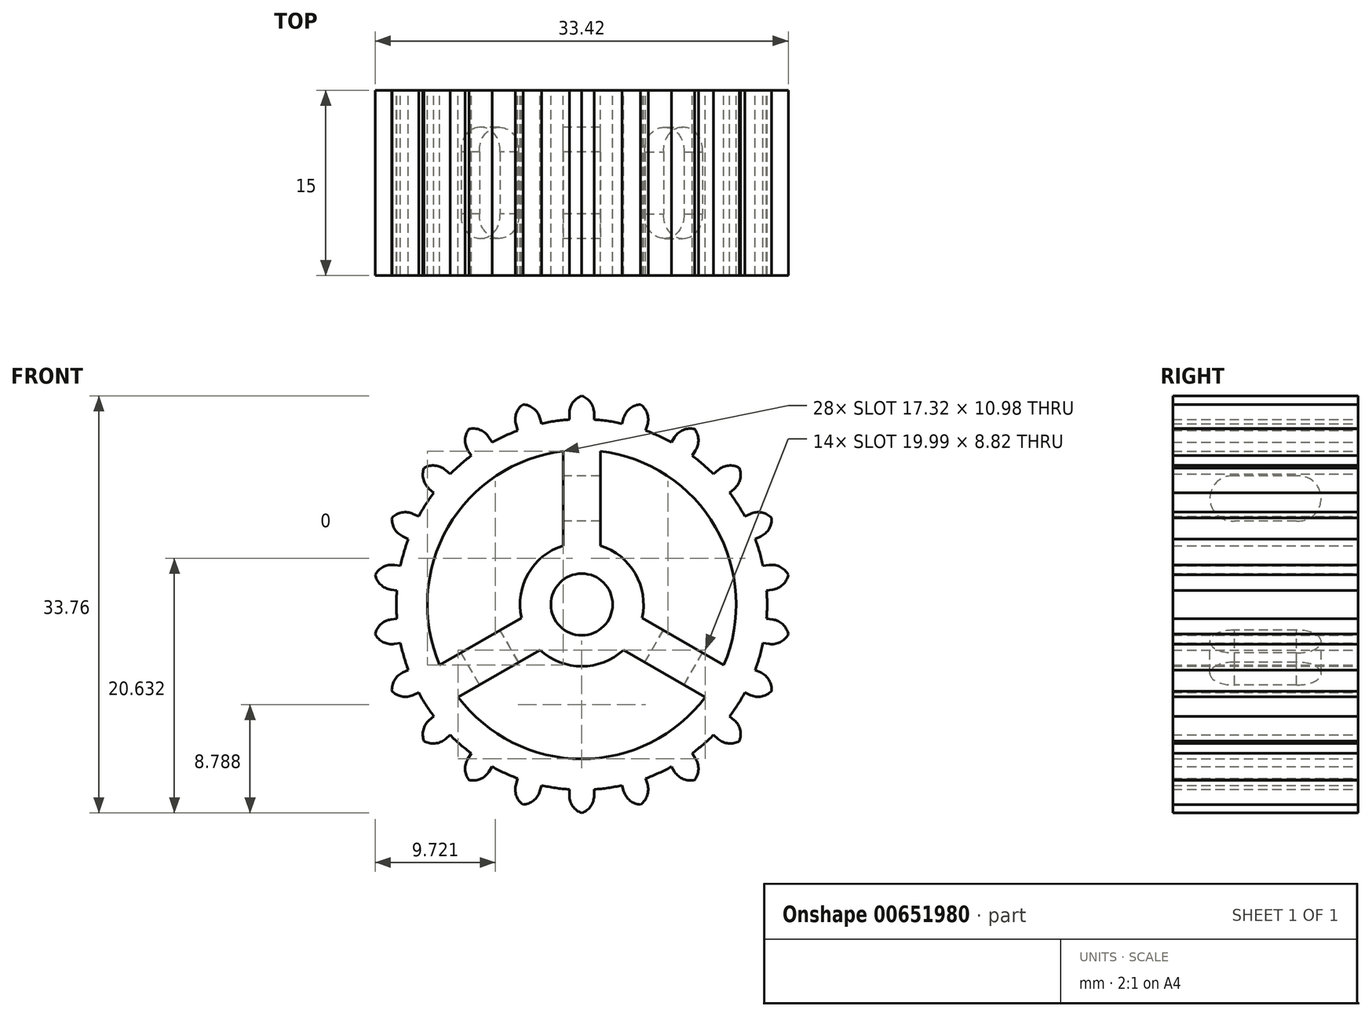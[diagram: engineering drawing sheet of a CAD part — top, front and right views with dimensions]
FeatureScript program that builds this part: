
annotation { "Feature Type Name" : "Feature", "Feature Type Description" : "" }
export const myFeature = defineFeature(function(context is Context, id is Id, definition is map)
    precondition{}
    {
        {
            var Q0;
            Q0=qCreatedBy(makeId("Front.planeOp"),FACE);
            var sketch = newSketch(context, id + "F0", { "sketchPlane" : qUnion([Q0])});
            skArc(sketch, "E0", {"start": v(-1, 14.97) * mm, "mid": v(-2.13, 14.85) * mm, "end": v(-3.26, 14.64) * mm});
            skLineSegment(sketch, "E1", {"start": v(-1, 14.97) * mm, "end": v(-1, 16.97) * mm});
            skLineSegment(sketch, "E2", {"start": v(-1, 16.97) * mm, "end": v(1, 16.97) * mm});
            skLineSegment(sketch, "E3", {"start": v(1, 16.97) * mm, "end": v(1, 14.97) * mm});
            skLineSegment(sketch, "E4.1.0", {"start": v(-3.82, 16.56) * mm, "end": v(-3.26, 14.64) * mm});
            skLineSegment(sketch, "E4.1.1", {"start": v(-5.18, 14.08) * mm, "end": v(-5.74, 16) * mm});
            skLineSegment(sketch, "E4.1.2", {"start": v(-5.74, 16) * mm, "end": v(-3.82, 16.56) * mm});
            skLineSegment(sketch, "E4.2.0", {"start": v(-8.33, 14.81) * mm, "end": v(-7.25, 13.13) * mm});
            skLineSegment(sketch, "E4.2.1", {"start": v(-8.93, 12.05) * mm, "end": v(-10.01, 13.73) * mm});
            skLineSegment(sketch, "E4.2.2", {"start": v(-10.01, 13.73) * mm, "end": v(-8.33, 14.81) * mm});
            skLineSegment(sketch, "E4.3.0", {"start": v(-12.17, 11.87) * mm, "end": v(-10.66, 10.56) * mm});
            skLineSegment(sketch, "E4.3.1", {"start": v(-11.97, 9.05) * mm, "end": v(-13.48, 10.36) * mm});
            skLineSegment(sketch, "E4.3.2", {"start": v(-13.48, 10.36) * mm, "end": v(-12.17, 11.87) * mm});
            skLineSegment(sketch, "E4.4.0", {"start": v(-15.02, 7.96) * mm, "end": v(-13.2, 7.13) * mm});
            skLineSegment(sketch, "E4.4.1", {"start": v(-14.03, 5.3) * mm, "end": v(-15.85, 6.14) * mm});
            skLineSegment(sketch, "E4.4.2", {"start": v(-15.85, 6.14) * mm, "end": v(-15.02, 7.96) * mm});
            skLineSegment(sketch, "E4.5.0", {"start": v(-16.65, 3.4) * mm, "end": v(-14.67, 3.12) * mm});
            skLineSegment(sketch, "E4.5.1", {"start": v(-14.96, 1.14) * mm, "end": v(-16.94, 1.42) * mm});
            skLineSegment(sketch, "E4.5.2", {"start": v(-16.94, 1.42) * mm, "end": v(-16.65, 3.4) * mm});
            skLineSegment(sketch, "E4.6.0", {"start": v(-16.94, -1.42) * mm, "end": v(-14.96, -1.14) * mm});
            skLineSegment(sketch, "E4.6.1", {"start": v(-14.67, -3.12) * mm, "end": v(-16.65, -3.4) * mm});
            skLineSegment(sketch, "E4.6.2", {"start": v(-16.65, -3.4) * mm, "end": v(-16.94, -1.42) * mm});
            skLineSegment(sketch, "E4.7.0", {"start": v(-15.85, -6.14) * mm, "end": v(-14.03, -5.3) * mm});
            skLineSegment(sketch, "E4.7.1", {"start": v(-13.2, -7.13) * mm, "end": v(-15.02, -7.96) * mm});
            skLineSegment(sketch, "E4.7.2", {"start": v(-15.02, -7.96) * mm, "end": v(-15.85, -6.14) * mm});
            skLineSegment(sketch, "E4.8.0", {"start": v(-13.48, -10.36) * mm, "end": v(-11.97, -9.05) * mm});
            skLineSegment(sketch, "E4.8.1", {"start": v(-10.66, -10.56) * mm, "end": v(-12.17, -11.87) * mm});
            skLineSegment(sketch, "E4.8.2", {"start": v(-12.17, -11.87) * mm, "end": v(-13.48, -10.36) * mm});
            skLineSegment(sketch, "E4.9.0", {"start": v(-10.01, -13.73) * mm, "end": v(-8.93, -12.05) * mm});
            skLineSegment(sketch, "E4.9.1", {"start": v(-7.25, -13.13) * mm, "end": v(-8.33, -14.81) * mm});
            skLineSegment(sketch, "E4.9.2", {"start": v(-8.33, -14.81) * mm, "end": v(-10.01, -13.73) * mm});
            skLineSegment(sketch, "E4.10.0", {"start": v(-5.74, -16) * mm, "end": v(-5.18, -14.08) * mm});
            skLineSegment(sketch, "E4.10.1", {"start": v(-3.26, -14.64) * mm, "end": v(-3.82, -16.56) * mm});
            skLineSegment(sketch, "E4.10.2", {"start": v(-3.82, -16.56) * mm, "end": v(-5.74, -16) * mm});
            skLineSegment(sketch, "E4.11.0", {"start": v(-1, -16.97) * mm, "end": v(-1, -14.97) * mm});
            skLineSegment(sketch, "E4.11.1", {"start": v(1, -14.97) * mm, "end": v(1, -16.97) * mm});
            skLineSegment(sketch, "E4.11.2", {"start": v(1, -16.97) * mm, "end": v(-1, -16.97) * mm});
            skLineSegment(sketch, "E4.12.0", {"start": v(3.82, -16.56) * mm, "end": v(3.26, -14.64) * mm});
            skLineSegment(sketch, "E4.12.1", {"start": v(5.18, -14.08) * mm, "end": v(5.74, -16) * mm});
            skLineSegment(sketch, "E4.12.2", {"start": v(5.74, -16) * mm, "end": v(3.82, -16.56) * mm});
            skLineSegment(sketch, "E4.13.0", {"start": v(8.33, -14.81) * mm, "end": v(7.25, -13.13) * mm});
            skLineSegment(sketch, "E4.13.1", {"start": v(8.93, -12.05) * mm, "end": v(10.01, -13.73) * mm});
            skLineSegment(sketch, "E4.13.2", {"start": v(10.01, -13.73) * mm, "end": v(8.33, -14.81) * mm});
            skLineSegment(sketch, "E4.14.0", {"start": v(12.17, -11.87) * mm, "end": v(10.66, -10.56) * mm});
            skLineSegment(sketch, "E4.14.1", {"start": v(11.97, -9.05) * mm, "end": v(13.48, -10.36) * mm});
            skLineSegment(sketch, "E4.14.2", {"start": v(13.48, -10.36) * mm, "end": v(12.17, -11.87) * mm});
            skLineSegment(sketch, "E4.15.0", {"start": v(15.02, -7.96) * mm, "end": v(13.2, -7.13) * mm});
            skLineSegment(sketch, "E4.15.1", {"start": v(14.03, -5.3) * mm, "end": v(15.85, -6.14) * mm});
            skLineSegment(sketch, "E4.15.2", {"start": v(15.85, -6.14) * mm, "end": v(15.02, -7.96) * mm});
            skLineSegment(sketch, "E4.16.0", {"start": v(16.65, -3.4) * mm, "end": v(14.67, -3.12) * mm});
            skLineSegment(sketch, "E4.16.1", {"start": v(14.96, -1.14) * mm, "end": v(16.94, -1.42) * mm});
            skLineSegment(sketch, "E4.16.2", {"start": v(16.94, -1.42) * mm, "end": v(16.65, -3.4) * mm});
            skLineSegment(sketch, "E4.17.0", {"start": v(16.94, 1.42) * mm, "end": v(14.96, 1.14) * mm});
            skLineSegment(sketch, "E4.17.1", {"start": v(14.67, 3.12) * mm, "end": v(16.65, 3.4) * mm});
            skLineSegment(sketch, "E4.17.2", {"start": v(16.65, 3.4) * mm, "end": v(16.94, 1.42) * mm});
            skLineSegment(sketch, "E4.18.0", {"start": v(15.85, 6.14) * mm, "end": v(14.03, 5.3) * mm});
            skLineSegment(sketch, "E4.18.1", {"start": v(13.2, 7.13) * mm, "end": v(15.02, 7.96) * mm});
            skLineSegment(sketch, "E4.18.2", {"start": v(15.02, 7.96) * mm, "end": v(15.85, 6.14) * mm});
            skLineSegment(sketch, "E4.19.0", {"start": v(13.48, 10.36) * mm, "end": v(11.97, 9.05) * mm});
            skLineSegment(sketch, "E4.19.1", {"start": v(10.66, 10.56) * mm, "end": v(12.17, 11.87) * mm});
            skLineSegment(sketch, "E4.19.2", {"start": v(12.17, 11.87) * mm, "end": v(13.48, 10.36) * mm});
            skLineSegment(sketch, "E4.20.0", {"start": v(10.01, 13.73) * mm, "end": v(8.93, 12.05) * mm});
            skLineSegment(sketch, "E4.20.1", {"start": v(7.25, 13.13) * mm, "end": v(8.33, 14.81) * mm});
            skLineSegment(sketch, "E4.20.2", {"start": v(8.33, 14.81) * mm, "end": v(10.01, 13.73) * mm});
            skLineSegment(sketch, "E4.21.0", {"start": v(5.74, 16) * mm, "end": v(5.18, 14.08) * mm});
            skLineSegment(sketch, "E4.21.1", {"start": v(3.26, 14.64) * mm, "end": v(3.82, 16.56) * mm});
            skLineSegment(sketch, "E4.21.2", {"start": v(3.82, 16.56) * mm, "end": v(5.74, 16) * mm});
            skArc(sketch, "E5.trimOffspring", {"start": v(3.26, 14.64) * mm, "mid": v(2.13, 14.85) * mm, "end": v(1, 14.97) * mm});
            skArc(sketch, "E6.trimOffspring", {"start": v(7.25, 13.13) * mm, "mid": v(6.23, 13.64) * mm, "end": v(5.18, 14.08) * mm});
            skArc(sketch, "E7.trimOffspring", {"start": v(10.66, 10.56) * mm, "mid": v(9.82, 11.34) * mm, "end": v(8.93, 12.05) * mm});
            skArc(sketch, "E8.trimOffspring", {"start": v(13.2, 7.13) * mm, "mid": v(12.62, 8.1) * mm, "end": v(11.97, 9.05) * mm});
            skArc(sketch, "E9.trimOffspring", {"start": v(14.67, 3.12) * mm, "mid": v(14.4, 4.23) * mm, "end": v(14.03, 5.3) * mm});
            skArc(sketch, "E10.trimOffspring", {"start": v(14.96, -1.14) * mm, "mid": v(15, 0) * mm, "end": v(14.96, 1.14) * mm});
            skArc(sketch, "E11.trimOffspring", {"start": v(14.03, -5.3) * mm, "mid": v(14.4, -4.23) * mm, "end": v(14.67, -3.12) * mm});
            skArc(sketch, "E12.trimOffspring", {"start": v(11.97, -9.05) * mm, "mid": v(12.62, -8.1) * mm, "end": v(13.2, -7.13) * mm});
            skArc(sketch, "E13.trimOffspring", {"start": v(8.93, -12.05) * mm, "mid": v(9.82, -11.34) * mm, "end": v(10.66, -10.56) * mm});
            skArc(sketch, "E14.trimOffspring", {"start": v(5.18, -14.08) * mm, "mid": v(6.23, -13.64) * mm, "end": v(7.25, -13.13) * mm});
            skArc(sketch, "E15.trimOffspring", {"start": v(1, -14.97) * mm, "mid": v(2.13, -14.85) * mm, "end": v(3.26, -14.64) * mm});
            skArc(sketch, "E16.trimOffspring", {"start": v(-3.26, -14.64) * mm, "mid": v(-2.13, -14.85) * mm, "end": v(-1, -14.97) * mm});
            skArc(sketch, "E17.trimOffspring", {"start": v(-7.25, -13.13) * mm, "mid": v(-6.23, -13.64) * mm, "end": v(-5.18, -14.08) * mm});
            skArc(sketch, "E18.trimOffspring", {"start": v(-10.66, -10.56) * mm, "mid": v(-9.82, -11.34) * mm, "end": v(-8.93, -12.05) * mm});
            skArc(sketch, "E19.trimOffspring", {"start": v(-13.2, -7.13) * mm, "mid": v(-12.62, -8.1) * mm, "end": v(-11.97, -9.05) * mm});
            skArc(sketch, "E20.trimOffspring", {"start": v(-14.67, -3.12) * mm, "mid": v(-14.4, -4.23) * mm, "end": v(-14.03, -5.3) * mm});
            skArc(sketch, "E21.trimOffspring", {"start": v(-14.96, 1.14) * mm, "mid": v(-15, 0) * mm, "end": v(-14.96, -1.14) * mm});
            skArc(sketch, "E22.trimOffspring", {"start": v(-14.03, 5.3) * mm, "mid": v(-14.4, 4.23) * mm, "end": v(-14.67, 3.12) * mm});
            skArc(sketch, "E23.trimOffspring", {"start": v(-11.97, 9.05) * mm, "mid": v(-12.62, 8.1) * mm, "end": v(-13.2, 7.13) * mm});
            skArc(sketch, "E24.trimOffspring", {"start": v(-8.93, 12.05) * mm, "mid": v(-9.82, 11.34) * mm, "end": v(-10.66, 10.56) * mm});
            skArc(sketch, "E25.trimOffspring", {"start": v(-5.18, 14.08) * mm, "mid": v(-6.23, 13.64) * mm, "end": v(-7.25, 13.13) * mm});
            skCircle(sketch, "E26", {"center": v(0, 0) * mm, "radius": 2.5 * mm});
            skArc(sketch, "E27", {"start": v(-1.5, 12.4) * mm, "mid": v(-10.83, 6.25) * mm, "end": v(-11.5, -4.9) * mm});
            skLineSegment(sketch, "E28", {"start": v(-1.5, 4.77) * mm, "end": v(-1.5, 12.4) * mm});
            skLineSegment(sketch, "E29", {"start": v(1.5, 12.4) * mm, "end": v(1.5, 4.77) * mm});
            skLineSegment(sketch, "E30.1.0", {"start": v(-3.38, -3.68) * mm, "end": v(-10, -7.5) * mm});
            skLineSegment(sketch, "E30.1.1", {"start": v(-11.5, -4.9) * mm, "end": v(-4.88, -1.09) * mm});
            skLineSegment(sketch, "E30.2.0", {"start": v(4.88, -1.09) * mm, "end": v(11.5, -4.9) * mm});
            skLineSegment(sketch, "E30.2.1", {"start": v(10, -7.5) * mm, "end": v(3.38, -3.68) * mm});
            skArc(sketch, "E31.trimOffspring", {"start": v(11.5, -4.9) * mm, "mid": v(10.83, 6.25) * mm, "end": v(1.5, 12.4) * mm});
            skArc(sketch, "E32.trimOffspring", {"start": v(-10, -7.5) * mm, "mid": v(0, -12.5) * mm, "end": v(10, -7.5) * mm});
            skArc(sketch, "E33", {"start": v(-3.38, -3.68) * mm, "mid": v(0, -5) * mm, "end": v(3.38, -3.68) * mm});
            skArc(sketch, "E34.trimOffspring", {"start": v(4.88, -1.09) * mm, "mid": v(4.33, 2.5) * mm, "end": v(1.5, 4.77) * mm});
            skArc(sketch, "E35.trimOffspring", {"start": v(-1.5, 4.77) * mm, "mid": v(-4.33, 2.5) * mm, "end": v(-4.88, -1.09) * mm});
            skPoint(sketch, "E36.orphan", {"position": v(-2.48, 0.3) * mm});
            skPoint(sketch, "E37.orphan", {"position": v(-1.5, 2) * mm});
            skPoint(sketch, "E38.orphan", {"position": v(1.5, 2) * mm});
            skPoint(sketch, "E39.orphan", {"position": v(2.48, 0.3) * mm});
            skPoint(sketch, "E40.orphan", {"position": v(0.98, -2.3) * mm});
            skPoint(sketch, "E41.orphan", {"position": v(-0.98, -2.3) * mm});
            skSolve(sketch);
        }
        {
            var Q0;
            Q0=makeQuery(id+"F0.imprint","IMPRINT",FACE,{"disambiguationData":[TD([[makeQuery(id+"F0.imprint","IMPRINT",EDGE,{"derivedFrom":sQuery(id+"F0.wireOp",EDGE,"E0")}),1.0]])]});
            var Q1;
            Q1=makeQuery(id+"F0.imprint","IMPRINT",FACE,{"disambiguationData":[TD([[makeQuery(id+"F0.imprint","IMPRINT",EDGE,{"derivedFrom":sQuery(id+"F0.wireOp",EDGE,"E1")}),-1.0]])]});
            extrude(context, id + "F1", {"entities" : qUnion([Q0, Q1]), "depth" : 15 * mm, "offsetDistance" : 25 * mm});
        }
        {
            var Q0;
            Q0=makeQuery(id+"F1.opExtrude","SWEPT_FACE",FACE,{"disambiguationData":[OSD([sQuery(id+"F0.wireOp",EDGE,"E30.2.0")])]});
            var sketch = newSketch(context, id + "F2", { "sketchPlane" : qUnion([Q0])});
            skArc(sketch, "E42", {"start": v(6.77, -10) * mm, "mid": v(8.59, -12) * mm, "end": v(10.4, -10) * mm});
            skArc(sketch, "E43", {"start": v(10.4, -5) * mm, "mid": v(8.59, -3) * mm, "end": v(6.77, -5) * mm});
            skLineSegment(sketch, "E44", {"start": v(6.77, -5) * mm, "end": v(6.77, -10) * mm});
            skLineSegment(sketch, "E45", {"start": v(10.4, -5) * mm, "end": v(10.4, -10) * mm});
            skSolve(sketch);
        }
        {
            var Q0;
            Q0=makeQuery(id+"F2.imprint","IMPRINT",FACE,{"disambiguationData":[TD([[makeQuery(id+"F2.imprint","IMPRINT",EDGE,{"derivedFrom":sQuery(id+"F2.wireOp",EDGE,"E42")}),1.0]])]});
            extrude(context, id + "F3", {"entities" : qUnion([Q0]), "operationType" : NewBodyOperationType.REMOVE, "endBound" : BoundingType.UP_TO_NEXT, "oppositeDirection" : true, "depth" : 25 * mm, "offsetDistance" : 25 * mm});
        }
        {
            var Q0;
            Q0=makeQuery(id+"F1.opExtrude","SWEPT_FACE",FACE,{"disambiguationData":[OSD([sQuery(id+"F0.wireOp",EDGE,"E30.1.1")])]});
            var sketch = newSketch(context, id + "F4", { "sketchPlane" : qUnion([Q0])});
            skArc(sketch, "E46", {"start": v(-10.4, -10) * mm, "mid": v(-8.59, -12) * mm, "end": v(-6.77, -10) * mm});
            skArc(sketch, "E47", {"start": v(-6.77, -5) * mm, "mid": v(-8.59, -3) * mm, "end": v(-10.4, -5) * mm});
            skLineSegment(sketch, "E48", {"start": v(-10.4, -5) * mm, "end": v(-10.4, -10) * mm});
            skLineSegment(sketch, "E49", {"start": v(-6.77, -5) * mm, "end": v(-6.77, -10) * mm});
            skSolve(sketch);
        }
        {
            var Q0;
            Q0=makeQuery(id+"F4.imprint","IMPRINT",FACE,{"disambiguationData":[TD([[makeQuery(id+"F4.imprint","IMPRINT",EDGE,{"derivedFrom":sQuery(id+"F4.wireOp",EDGE,"E46")}),1.0]])]});
            extrude(context, id + "F5", {"entities" : qUnion([Q0]), "operationType" : NewBodyOperationType.REMOVE, "endBound" : BoundingType.UP_TO_NEXT, "oppositeDirection" : true, "depth" : 25 * mm, "offsetDistance" : 25 * mm});
        }
        {
            var Q0;
            Q0=makeQuery(id+"F1.opExtrude","SWEPT_FACE",FACE,{"disambiguationData":[OSD([sQuery(id+"F0.wireOp",EDGE,"E28")])]});
            var sketch = newSketch(context, id + "F6", { "sketchPlane" : qUnion([Q0])});
            skArc(sketch, "E50", {"start": v(5, 10.4) * mm, "mid": v(3, 8.59) * mm, "end": v(5, 6.77) * mm});
            skArc(sketch, "E51", {"start": v(10, 6.77) * mm, "mid": v(12, 8.59) * mm, "end": v(10, 10.4) * mm});
            skLineSegment(sketch, "E52", {"start": v(5, 6.77) * mm, "end": v(10, 6.77) * mm});
            skLineSegment(sketch, "E53", {"start": v(5, 10.4) * mm, "end": v(10, 10.4) * mm});
            skSolve(sketch);
        }
        {
            var Q0;
            Q0=makeQuery(id+"F6.imprint","IMPRINT",FACE,{"disambiguationData":[TD([[makeQuery(id+"F6.imprint","IMPRINT",EDGE,{"derivedFrom":sQuery(id+"F6.wireOp",EDGE,"E50")}),1.0]])]});
            extrude(context, id + "F7", {"entities" : qUnion([Q0]), "operationType" : NewBodyOperationType.REMOVE, "endBound" : BoundingType.UP_TO_NEXT, "oppositeDirection" : true, "depth" : 25 * mm, "offsetDistance" : 25 * mm});
        }
        {
            var Q0;
            Q0=makeQuery(id+"F1.opExtrude","SWEPT_EDGE",EDGE,{"disambiguationData":[OSD([sQuery(id+"F0.wireOp",EDGE,"E4.8.1"),sQuery(id+"F0.wireOp",EDGE,"E4.8.2")])]});
            var Q1;
            Q1=makeQuery(id+"F1.opExtrude","SWEPT_EDGE",EDGE,{"disambiguationData":[OSD([sQuery(id+"F0.wireOp",EDGE,"E4.8.0"),sQuery(id+"F0.wireOp",EDGE,"E4.8.2")])]});
            var Q2;
            Q2=makeQuery(id+"F1.opExtrude","SWEPT_EDGE",EDGE,{"disambiguationData":[OSD([sQuery(id+"F0.wireOp",EDGE,"E4.7.1"),sQuery(id+"F0.wireOp",EDGE,"E4.7.2")])]});
            var Q3;
            Q3=makeQuery(id+"F1.opExtrude","SWEPT_EDGE",EDGE,{"disambiguationData":[OSD([sQuery(id+"F0.wireOp",EDGE,"E4.7.0"),sQuery(id+"F0.wireOp",EDGE,"E4.7.2")])]});
            var Q4;
            Q4=makeQuery(id+"F1.opExtrude","SWEPT_EDGE",EDGE,{"disambiguationData":[OSD([sQuery(id+"F0.wireOp",EDGE,"E4.6.0"),sQuery(id+"F0.wireOp",EDGE,"E4.6.2")])]});
            var Q5;
            Q5=makeQuery(id+"F1.opExtrude","SWEPT_EDGE",EDGE,{"disambiguationData":[OSD([sQuery(id+"F0.wireOp",EDGE,"E4.6.1"),sQuery(id+"F0.wireOp",EDGE,"E4.6.2")])]});
            var Q6;
            Q6=makeQuery(id+"F1.opExtrude","SWEPT_EDGE",EDGE,{"disambiguationData":[OSD([sQuery(id+"F0.wireOp",EDGE,"E4.5.0"),sQuery(id+"F0.wireOp",EDGE,"E4.5.2")])]});
            var Q7;
            Q7=makeQuery(id+"F1.opExtrude","SWEPT_EDGE",EDGE,{"disambiguationData":[OSD([sQuery(id+"F0.wireOp",EDGE,"E4.5.1"),sQuery(id+"F0.wireOp",EDGE,"E4.5.2")])]});
            var Q8;
            Q8=makeQuery(id+"F1.opExtrude","SWEPT_EDGE",EDGE,{"disambiguationData":[OSD([sQuery(id+"F0.wireOp",EDGE,"E4.4.0"),sQuery(id+"F0.wireOp",EDGE,"E4.4.2")])]});
            var Q9;
            Q9=makeQuery(id+"F1.opExtrude","SWEPT_EDGE",EDGE,{"disambiguationData":[OSD([sQuery(id+"F0.wireOp",EDGE,"E4.4.1"),sQuery(id+"F0.wireOp",EDGE,"E4.4.2")])]});
            var Q10;
            Q10=makeQuery(id+"F1.opExtrude","SWEPT_EDGE",EDGE,{"disambiguationData":[OSD([sQuery(id+"F0.wireOp",EDGE,"E4.3.0"),sQuery(id+"F0.wireOp",EDGE,"E4.3.2")])]});
            var Q11;
            Q11=makeQuery(id+"F1.opExtrude","SWEPT_EDGE",EDGE,{"disambiguationData":[OSD([sQuery(id+"F0.wireOp",EDGE,"E4.3.1"),sQuery(id+"F0.wireOp",EDGE,"E4.3.2")])]});
            var Q12;
            Q12=makeQuery(id+"F1.opExtrude","SWEPT_EDGE",EDGE,{"disambiguationData":[OSD([sQuery(id+"F0.wireOp",EDGE,"E4.2.0"),sQuery(id+"F0.wireOp",EDGE,"E4.2.2")])]});
            var Q13;
            Q13=makeQuery(id+"F1.opExtrude","SWEPT_EDGE",EDGE,{"disambiguationData":[OSD([sQuery(id+"F0.wireOp",EDGE,"E4.2.1"),sQuery(id+"F0.wireOp",EDGE,"E4.2.2")])]});
            var Q14;
            Q14=makeQuery(id+"F1.opExtrude","SWEPT_EDGE",EDGE,{"disambiguationData":[OSD([sQuery(id+"F0.wireOp",EDGE,"E4.1.1"),sQuery(id+"F0.wireOp",EDGE,"E4.1.2")])]});
            var Q15;
            Q15=makeQuery(id+"F1.opExtrude","SWEPT_EDGE",EDGE,{"disambiguationData":[OSD([sQuery(id+"F0.wireOp",EDGE,"E4.1.0"),sQuery(id+"F0.wireOp",EDGE,"E4.1.2")])]});
            var Q16;
            Q16=makeQuery(id+"F1.opExtrude","SWEPT_EDGE",EDGE,{"disambiguationData":[OSD([sQuery(id+"F0.wireOp",EDGE,"E1"),sQuery(id+"F0.wireOp",EDGE,"E2")])]});
            var Q17;
            Q17=makeQuery(id+"F1.opExtrude","SWEPT_EDGE",EDGE,{"disambiguationData":[OSD([sQuery(id+"F0.wireOp",EDGE,"E2"),sQuery(id+"F0.wireOp",EDGE,"E3")])]});
            var Q18;
            Q18=makeQuery(id+"F1.opExtrude","SWEPT_EDGE",EDGE,{"disambiguationData":[OSD([sQuery(id+"F0.wireOp",EDGE,"E4.21.1"),sQuery(id+"F0.wireOp",EDGE,"E4.21.2")])]});
            var Q19;
            Q19=makeQuery(id+"F1.opExtrude","SWEPT_EDGE",EDGE,{"disambiguationData":[OSD([sQuery(id+"F0.wireOp",EDGE,"E4.21.0"),sQuery(id+"F0.wireOp",EDGE,"E4.21.2")])]});
            var Q20;
            Q20=makeQuery(id+"F1.opExtrude","SWEPT_EDGE",EDGE,{"disambiguationData":[OSD([sQuery(id+"F0.wireOp",EDGE,"E4.20.1"),sQuery(id+"F0.wireOp",EDGE,"E4.20.2")])]});
            var Q21;
            Q21=makeQuery(id+"F1.opExtrude","SWEPT_EDGE",EDGE,{"disambiguationData":[OSD([sQuery(id+"F0.wireOp",EDGE,"E4.20.0"),sQuery(id+"F0.wireOp",EDGE,"E4.20.2")])]});
            var Q22;
            Q22=makeQuery(id+"F1.opExtrude","SWEPT_EDGE",EDGE,{"disambiguationData":[OSD([sQuery(id+"F0.wireOp",EDGE,"E4.19.1"),sQuery(id+"F0.wireOp",EDGE,"E4.19.2")])]});
            var Q23;
            Q23=makeQuery(id+"F1.opExtrude","SWEPT_EDGE",EDGE,{"disambiguationData":[OSD([sQuery(id+"F0.wireOp",EDGE,"E4.19.0"),sQuery(id+"F0.wireOp",EDGE,"E4.19.2")])]});
            var Q24;
            Q24=makeQuery(id+"F1.opExtrude","SWEPT_EDGE",EDGE,{"disambiguationData":[OSD([sQuery(id+"F0.wireOp",EDGE,"E4.18.0"),sQuery(id+"F0.wireOp",EDGE,"E4.18.2")])]});
            var Q25;
            Q25=makeQuery(id+"F1.opExtrude","SWEPT_EDGE",EDGE,{"disambiguationData":[OSD([sQuery(id+"F0.wireOp",EDGE,"E4.18.1"),sQuery(id+"F0.wireOp",EDGE,"E4.18.2")])]});
            var Q26;
            Q26=makeQuery(id+"F1.opExtrude","SWEPT_EDGE",EDGE,{"disambiguationData":[OSD([sQuery(id+"F0.wireOp",EDGE,"E4.17.0"),sQuery(id+"F0.wireOp",EDGE,"E4.17.2")])]});
            var Q27;
            Q27=makeQuery(id+"F1.opExtrude","SWEPT_EDGE",EDGE,{"disambiguationData":[OSD([sQuery(id+"F0.wireOp",EDGE,"E4.17.1"),sQuery(id+"F0.wireOp",EDGE,"E4.17.2")])]});
            var Q28;
            Q28=makeQuery(id+"F1.opExtrude","SWEPT_EDGE",EDGE,{"disambiguationData":[OSD([sQuery(id+"F0.wireOp",EDGE,"E4.16.0"),sQuery(id+"F0.wireOp",EDGE,"E4.16.2")])]});
            var Q29;
            Q29=makeQuery(id+"F1.opExtrude","SWEPT_EDGE",EDGE,{"disambiguationData":[OSD([sQuery(id+"F0.wireOp",EDGE,"E4.16.1"),sQuery(id+"F0.wireOp",EDGE,"E4.16.2")])]});
            var Q30;
            Q30=makeQuery(id+"F1.opExtrude","SWEPT_EDGE",EDGE,{"disambiguationData":[OSD([sQuery(id+"F0.wireOp",EDGE,"E4.15.1"),sQuery(id+"F0.wireOp",EDGE,"E4.15.2")])]});
            var Q31;
            Q31=makeQuery(id+"F1.opExtrude","SWEPT_EDGE",EDGE,{"disambiguationData":[OSD([sQuery(id+"F0.wireOp",EDGE,"E4.15.0"),sQuery(id+"F0.wireOp",EDGE,"E4.15.2")])]});
            var Q32;
            Q32=makeQuery(id+"F1.opExtrude","SWEPT_EDGE",EDGE,{"disambiguationData":[OSD([sQuery(id+"F0.wireOp",EDGE,"E4.14.1"),sQuery(id+"F0.wireOp",EDGE,"E4.14.2")])]});
            var Q33;
            Q33=makeQuery(id+"F1.opExtrude","SWEPT_EDGE",EDGE,{"disambiguationData":[OSD([sQuery(id+"F0.wireOp",EDGE,"E4.14.0"),sQuery(id+"F0.wireOp",EDGE,"E4.14.2")])]});
            var Q34;
            Q34=makeQuery(id+"F1.opExtrude","SWEPT_EDGE",EDGE,{"disambiguationData":[OSD([sQuery(id+"F0.wireOp",EDGE,"E4.13.1"),sQuery(id+"F0.wireOp",EDGE,"E4.13.2")])]});
            var Q35;
            Q35=makeQuery(id+"F1.opExtrude","SWEPT_EDGE",EDGE,{"disambiguationData":[OSD([sQuery(id+"F0.wireOp",EDGE,"E4.13.0"),sQuery(id+"F0.wireOp",EDGE,"E4.13.2")])]});
            var Q36;
            Q36=makeQuery(id+"F1.opExtrude","SWEPT_EDGE",EDGE,{"disambiguationData":[OSD([sQuery(id+"F0.wireOp",EDGE,"E4.12.1"),sQuery(id+"F0.wireOp",EDGE,"E4.12.2")])]});
            var Q37;
            Q37=makeQuery(id+"F1.opExtrude","SWEPT_EDGE",EDGE,{"disambiguationData":[OSD([sQuery(id+"F0.wireOp",EDGE,"E4.12.0"),sQuery(id+"F0.wireOp",EDGE,"E4.12.2")])]});
            var Q38;
            Q38=makeQuery(id+"F1.opExtrude","SWEPT_EDGE",EDGE,{"disambiguationData":[OSD([sQuery(id+"F0.wireOp",EDGE,"E4.11.1"),sQuery(id+"F0.wireOp",EDGE,"E4.11.2")])]});
            var Q39;
            Q39=makeQuery(id+"F1.opExtrude","SWEPT_EDGE",EDGE,{"disambiguationData":[OSD([sQuery(id+"F0.wireOp",EDGE,"E4.11.0"),sQuery(id+"F0.wireOp",EDGE,"E4.11.2")])]});
            var Q40;
            Q40=makeQuery(id+"F1.opExtrude","SWEPT_EDGE",EDGE,{"disambiguationData":[OSD([sQuery(id+"F0.wireOp",EDGE,"E4.10.1"),sQuery(id+"F0.wireOp",EDGE,"E4.10.2")])]});
            var Q41;
            Q41=makeQuery(id+"F1.opExtrude","SWEPT_EDGE",EDGE,{"disambiguationData":[OSD([sQuery(id+"F0.wireOp",EDGE,"E4.10.0"),sQuery(id+"F0.wireOp",EDGE,"E4.10.2")])]});
            var Q42;
            Q42=makeQuery(id+"F1.opExtrude","SWEPT_EDGE",EDGE,{"disambiguationData":[OSD([sQuery(id+"F0.wireOp",EDGE,"E4.9.1"),sQuery(id+"F0.wireOp",EDGE,"E4.9.2")])]});
            var Q43;
            Q43=makeQuery(id+"F1.opExtrude","SWEPT_EDGE",EDGE,{"disambiguationData":[OSD([sQuery(id+"F0.wireOp",EDGE,"E4.9.0"),sQuery(id+"F0.wireOp",EDGE,"E4.9.2")])]});
            fillet(context, id + "F8", {"entities" : qUnion([Q0, Q1, Q2, Q3, Q4, Q5, Q6, Q7, Q8, Q9, Q10, Q11, Q12, Q13, Q14, Q15, Q16, Q17, Q18, Q19, Q20, Q21, Q22, Q23, Q24, Q25, Q26, Q27, Q28, Q29, Q30, Q31, Q32, Q33, Q34, Q35, Q36, Q37, Q38, Q39, Q40, Q41, Q42, Q43]), "radius" : 1.5 * mm, "tangentPropagation" : true, "allowEdgeOverflow" : false});
        }
    });
